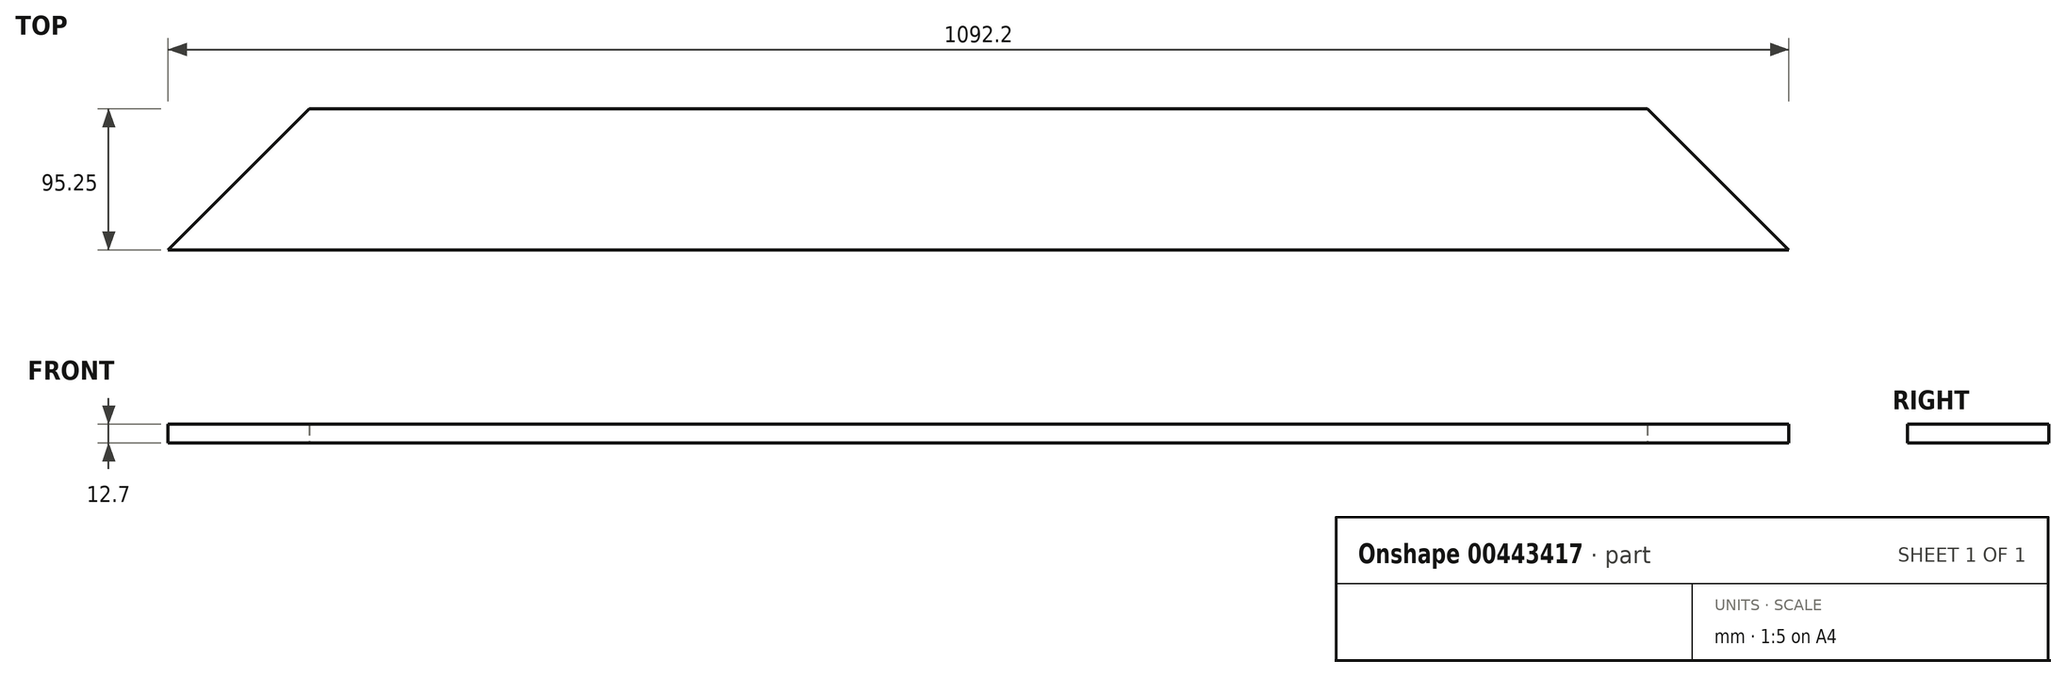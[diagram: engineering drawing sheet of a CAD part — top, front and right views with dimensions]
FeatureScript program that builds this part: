
annotation { "Feature Type Name" : "Feature", "Feature Type Description" : "" }
export const myFeature = defineFeature(function(context is Context, id is Id, definition is map)
    precondition{}
    {
        {
            var Q0;
            Q0=qCreatedBy(makeId("Top.planeOp"),FACE);
            var sketch = newSketch(context, id + "F0", { "sketchPlane" : qUnion([Q0])});
            skLineSegment(sketch, "E0", {"start": v(-482.54, -50.95) * mm, "end": v(609.66, -50.95) * mm});
            skLineSegment(sketch, "E1", {"start": v(-387.29, 44.3) * mm, "end": v(514.41, 44.3) * mm});
            skLineSegment(sketch, "E2", {"start": v(-387.29, 44.3) * mm, "end": v(-482.54, -50.95) * mm});
            skLineSegment(sketch, "E3", {"start": v(514.41, 44.3) * mm, "end": v(609.66, -50.95) * mm});
            skSolve(sketch);
        }
        {
            var Q0;
            Q0 = qSketchRegion(id + "F0", true);
            extrude(context, id + "F1", {"entities" : qUnion([Q0]), "depth" : 12.7 * mm});
        }
    });
